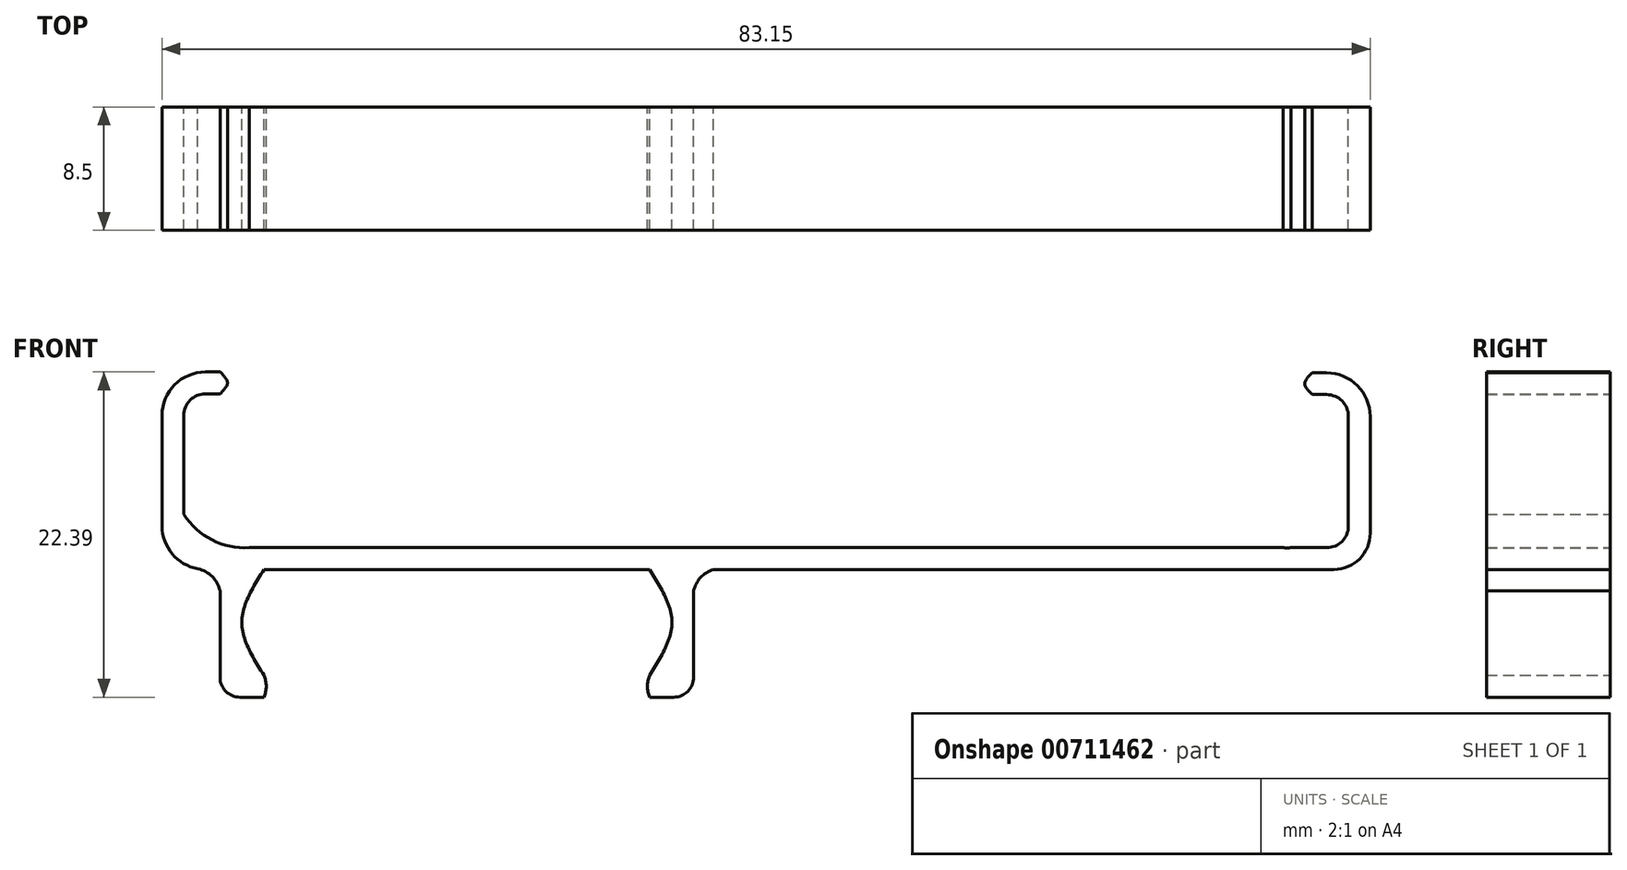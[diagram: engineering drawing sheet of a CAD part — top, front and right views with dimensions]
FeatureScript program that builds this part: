
annotation { "Feature Type Name" : "Feature", "Feature Type Description" : "" }
export const myFeature = defineFeature(function(context is Context, id is Id, definition is map)
    precondition{}
    {
        {
            var Q0;
            Q0=qCreatedBy(makeId("Front.planeOp"),FACE);
            var sketch = newSketch(context, id + "F0", { "sketchPlane" : qUnion([Q0])});
            skLineSegment(sketch, "E0", {"start": v(-20.82, 0) * mm, "end": v(56.33, 0) * mm});
            skPoint(sketch, "E1.visualSharp", {"position": v(-22.32, 10.6) * mm});
            skPoint(sketch, "E2.visualSharp", {"position": v(57.83, 10.54) * mm});
            skPoint(sketch, "E3.visualSharp", {"position": v(57.68, 0) * mm});
            skArc(sketch, "E3.filletArc", {"start": v(56.33, 0) * mm, "mid": v(57.39, 0.44) * mm, "end": v(57.83, 1.5) * mm});
            skPoint(sketch, "E4.visualSharp", {"position": v(-22.32, 0) * mm});
            skArc(sketch, "E4.filletArc", {"start": v(-22.32, 1.5) * mm, "mid": v(-21.88, 0.44) * mm, "end": v(-20.82, 0) * mm});
            skArc(sketch, "E5.0", {"start": v(-23.82, 1.5) * mm, "mid": v(-22.8, -0.76) * mm, "end": v(-20.42, -1.47) * mm});
            skLineSegment(sketch, "E6.0", {"start": v(-18.33, -1.5) * mm, "end": v(56.58, -1.5) * mm});
            skLineSegment(sketch, "E7", {"start": v(-22.32, 1.5) * mm, "end": v(-22.32, -1.1) * mm, "construction": true});
            skLineSegment(sketch, "E8", {"start": v(-19.83, -2.98) * mm, "end": v(-18.33, -2.98) * mm, "construction": true});
            skLineSegment(sketch, "E9", {"start": v(-18.33, -1.5) * mm, "end": v(-18.33, -8.79) * mm});
            skLineSegment(sketch, "E10", {"start": v(-18.33, -8.79) * mm, "end": v(-16.81, -8.79) * mm});
            skLineSegment(sketch, "E11", {"start": v(-20.42, -1.47) * mm, "end": v(-18.33, -1.5) * mm});
            skFitSpline(sketch, "E12", {"points": [v(-16.81, -8.79) * mm, v(-18.33, -5.14) * mm, v(-16.81, -1.5) * mm], "startDerivative": vector(-4.56, 7.29) * mm, "endDerivative": vector(4.56, 7.29) * mm});
            skLineSegment(sketch, "E13.0", {"start": v(-18.33, -10.29) * mm, "end": v(-16.81, -10.29) * mm});
            skLineSegment(sketch, "E14.0", {"start": v(-19.83, -1.5) * mm, "end": v(-19.83, -8.79) * mm});
            skLineSegment(sketch, "E15", {"start": v(-19.83, -8.79) * mm, "end": v(-19.83, -8.91) * mm});
            skLineSegment(sketch, "E16", {"start": v(-18.33, -10.29) * mm, "end": v(-18.46, -10.29) * mm});
            skArc(sketch, "E17", {"start": v(-19.83, -2.98) * mm, "mid": v(-20.4, -1.96) * mm, "end": v(-21.43, -1.44) * mm});
            skArc(sketch, "E18", {"start": v(-16.81, -10.29) * mm, "mid": v(-16.65, -9.54) * mm, "end": v(-16.81, -8.79) * mm});
            skPoint(sketch, "E19.visualSharp", {"position": v(-19.83, -10.29) * mm});
            skArc(sketch, "E19.filletArc", {"start": v(-19.83, -8.91) * mm, "mid": v(-19.43, -9.89) * mm, "end": v(-18.46, -10.29) * mm});
            skLineSegment(sketch, "E20", {"start": v(-18.33, -5.14) * mm, "end": v(-3.33, -5.14) * mm, "construction": true});
            skPoint(sketch, "E21.start.orphan", {"position": v(-3.33, -1.5) * mm});
            skLineSegment(sketch, "E22", {"start": v(-3.33, -1.5) * mm, "end": v(-3.33, -10.67) * mm, "construction": true});
            skLineSegment(sketch, "E23.MirrorCS", {"start": v(11.27, -10.29) * mm, "end": v(11.39, -10.29) * mm});
            skLineSegment(sketch, "E24.MirrorCS", {"start": v(12.77, -8.79) * mm, "end": v(12.77, -8.91) * mm});
            skLineSegment(sketch, "E25.MirrorCS", {"start": v(11.27, -8.79) * mm, "end": v(9.74, -8.79) * mm});
            skArc(sketch, "E26.MirrorCS", {"start": v(12.77, -8.91) * mm, "mid": v(12.36, -9.89) * mm, "end": v(11.39, -10.29) * mm});
            skLineSegment(sketch, "E27.MirrorCS", {"start": v(11.27, -10.29) * mm, "end": v(9.74, -10.29) * mm});
            skPoint(sketch, "E28.MirrorP", {"position": v(12.77, -10.29) * mm});
            skLineSegment(sketch, "E29.MirrorCS", {"start": v(11.67, -5.14) * mm, "end": v(-3.33, -5.14) * mm, "construction": true});
            skLineSegment(sketch, "E30.MirrorCS", {"start": v(12.77, -1.5) * mm, "end": v(12.77, -8.79) * mm});
            skFitSpline(sketch, "E31.MirrorCS", {"points": [v(9.74, -8.79) * mm, v(11.27, -5.14) * mm, v(9.74, -1.5) * mm], "startDerivative": vector(4.56, 7.29) * mm, "endDerivative": vector(-4.56, 7.29) * mm});
            skLineSegment(sketch, "E32.MirrorCS", {"start": v(11.27, -1.5) * mm, "end": v(11.27, -8.79) * mm});
            skArc(sketch, "E33.MirrorCS", {"start": v(9.74, -10.29) * mm, "mid": v(9.59, -9.54) * mm, "end": v(9.74, -8.79) * mm});
            skLineSegment(sketch, "E34.MirrorCS", {"start": v(12.77, -2.98) * mm, "end": v(11.27, -2.98) * mm, "construction": true});
            skArc(sketch, "E35.MirrorCS", {"start": v(12.77, -2.98) * mm, "mid": v(13.33, -1.96) * mm, "end": v(14.37, -1.44) * mm});
            skLineSegment(sketch, "E36", {"start": v(59.33, 1.4) * mm, "end": v(59.33, 1) * mm});
            skLineSegment(sketch, "E37", {"start": v(56.83, -1.5) * mm, "end": v(56.58, -1.5) * mm});
            skPoint(sketch, "E38.visualSharp", {"position": v(59.33, -1.5) * mm});
            skArc(sketch, "E38.filletArc", {"start": v(56.83, -1.5) * mm, "mid": v(58.6, -0.77) * mm, "end": v(59.33, 1) * mm});
            skLineSegment(sketch, "E39", {"start": v(-20.82, 10.6) * mm, "end": v(-19.82, 10.6) * mm});
            skLineSegment(sketch, "E40", {"start": v(-19.82, 10.6) * mm, "end": v(-19.82, 12.1) * mm, "construction": true});
            skFitSpline(sketch, "E41", {"points": [v(-19.82, 12.1) * mm, v(-19.32, 11.35) * mm, v(-19.82, 10.6) * mm], "startDerivative": vector(1.5, -1.5) * mm, "endDerivative": vector(-1.5, -1.5) * mm});
            skLineSegment(sketch, "E42", {"start": v(-22.32, 1.5) * mm, "end": v(-22.32, 9.1) * mm});
            skLineSegment(sketch, "E43", {"start": v(-19.82, 12.1) * mm, "end": v(-20.82, 12.1) * mm});
            skLineSegment(sketch, "E44", {"start": v(-23.82, 9.1) * mm, "end": v(-23.82, 1.5) * mm});
            skArc(sketch, "E45.filletArc", {"start": v(-20.82, 10.6) * mm, "mid": v(-21.88, 10.16) * mm, "end": v(-22.32, 9.1) * mm});
            skPoint(sketch, "E46.visualSharp", {"position": v(-23.82, 12.1) * mm});
            skArc(sketch, "E46.filletArc", {"start": v(-20.82, 12.1) * mm, "mid": v(-22.94, 11.22) * mm, "end": v(-23.82, 9.1) * mm});
            skLineSegment(sketch, "E47", {"start": v(57.83, 1.5) * mm, "end": v(57.83, 9.04) * mm});
            skLineSegment(sketch, "E48.trimOffspring", {"start": v(55.33, 10.54) * mm, "end": v(56.33, 10.54) * mm});
            skLineSegment(sketch, "E49", {"start": v(55.33, 12.04) * mm, "end": v(55.33, 10.54) * mm});
            skLineSegment(sketch, "E50", {"start": v(59.33, 1.4) * mm, "end": v(59.33, 9.04) * mm});
            skLineSegment(sketch, "E51", {"start": v(55.33, 12.04) * mm, "end": v(56.33, 12.04) * mm});
            skArc(sketch, "E52.filletArc", {"start": v(57.83, 9.04) * mm, "mid": v(57.39, 10.1) * mm, "end": v(56.33, 10.54) * mm});
            skPoint(sketch, "E53.visualSharp", {"position": v(59.33, 12.04) * mm});
            skArc(sketch, "E53.filletArc", {"start": v(59.33, 9.04) * mm, "mid": v(58.45, 11.16) * mm, "end": v(56.33, 12.04) * mm});
            skLineSegment(sketch, "E54", {"start": v(-19.32, 11.35) * mm, "end": v(-19.82, 11.35) * mm, "construction": true});
            skPoint(sketch, "E55.start.orphan", {"position": v(55.33, 11.3) * mm});
            skLineSegment(sketch, "E56", {"start": v(55.33, 11.3) * mm, "end": v(54.83, 11.3) * mm, "construction": true});
            skFitSpline(sketch, "E57", {"points": [v(55.33, 12.04) * mm, v(54.83, 11.3) * mm, v(55.33, 10.54) * mm], "startDerivative": vector(-1.5, -1.5) * mm, "endDerivative": vector(1.5, -1.5) * mm});
            skLineSegment(sketch, "E58", {"start": v(-22.32, 5.3) * mm, "end": v(57.83, 5.3) * mm, "construction": true});
            skPoint(sketch, "E59.end.orphan", {"position": v(-19.82, 6.72) * mm});
            skLineSegment(sketch, "E60", {"start": v(-19.82, 10.6) * mm, "end": v(-19.82, 0) * mm, "construction": true});
            skLineSegment(sketch, "E61", {"start": v(55.33, 10.54) * mm, "end": v(55.33, 0) * mm, "construction": true});
            skLineSegment(sketch, "E62", {"start": v(-20.82, 2.3) * mm, "end": v(-22.32, 2.3) * mm, "construction": true});
            skLineSegment(sketch, "E63", {"start": v(-22.32, 2.3) * mm, "end": v(-17.82, 2.3) * mm, "construction": true});
            skArc(sketch, "E64", {"start": v(-22.32, 2.3) * mm, "mid": v(-20.39, 0.54) * mm, "end": v(-17.82, 0) * mm});
            skLineSegment(sketch, "E65", {"start": v(57.83, 2.3) * mm, "end": v(53.33, 2.3) * mm, "construction": true});
            skArc(sketch, "E66", {"start": v(53.33, 0) * mm, "mid": v(55.9, 0.54) * mm, "end": v(57.83, 2.3) * mm});
            skSolve(sketch);
        }
        {
            var Q0;
            Q0=makeQuery(id+"F0.imprint","IMPRINT",FACE,{"disambiguationData":[TD([[makeQuery(id+"F0.imprint","IMPRINT",EDGE,{"derivedFrom":sQuery(id+"F0.wireOp",EDGE,"E23.MirrorCS")}),1.0]])]});
            var Q1;
            {var subQ9=sQuery(id+"F0.wireOp",EDGE,"E10");Q1=makeQuery(id+"F0.imprint","IMPRINT",FACE,{"disambiguationData":[TD([[makeQuery(id+"F0.imprint","IMPRINT",EDGE,{"derivedFrom":subQ9}),-1.0]])]});}
            var Q2;
            {var subQ0=sQuery(id+"F0.wireOp",EDGE,"E30.MirrorCS");var subQ1=sQuery(id+"F0.wireOp",EDGE,"E6.0");var subQ2=makeQuery(id+"F0.imprint","INTERSECT",VERTEX,{"derivedFrom":[subQ1,subQ0]});Q2=makeQuery(id+"F0.imprint","IMPRINT",FACE,{"disambiguationData":[TD([[makeQuery(id+"F0.imprint","IMPRINT",EDGE,{"disambiguationData":[TD([[subQ2,-1.0]])],"derivedFrom":subQ1}),-1.0]])]});}
            var Q3;
            {var subQ0=sQuery(id+"F0.wireOp",EDGE,"E10");Q3=makeQuery(id+"F0.imprint","IMPRINT",FACE,{"disambiguationData":[TD([[makeQuery(id+"F0.imprint","IMPRINT",EDGE,{"derivedFrom":subQ0}),1.0]])]});}
            var Q4;
            {var subQ0=sQuery(id+"F0.wireOp",EDGE,"E31.MirrorCS");var subQ1=sQuery(id+"F0.wireOp",EDGE,"E6.0");var subQ2=makeQuery(id+"F0.imprint","INTERSECT",VERTEX,{"derivedFrom":[subQ1,subQ0]});Q4=makeQuery(id+"F0.imprint","IMPRINT",FACE,{"disambiguationData":[TD([[makeQuery(id+"F0.imprint","IMPRINT",EDGE,{"disambiguationData":[TD([[subQ2,-1.0]])],"derivedFrom":subQ1}),-1.0]])]});}
            var Q5;
            {var subQ0=sQuery(id+"F0.wireOp",EDGE,"E17");var subQ1=sQuery(id+"F0.wireOp",EDGE,"E5.0");var subQ2=makeQuery(id+"F0.imprint","INTERSECT",VERTEX,{"disambiguationData":[OD(0.0)],"derivedFrom":[subQ1,subQ0]});Q5=makeQuery(id+"F0.imprint","IMPRINT",FACE,{"disambiguationData":[TD([[makeQuery(id+"F0.imprint","IMPRINT",EDGE,{"disambiguationData":[TD([[subQ2,-1.0]])],"derivedFrom":subQ1}),1.0]])]});}
            var Q6;
            Q6=makeQuery(id+"F0.imprint","IMPRINT",FACE,{"disambiguationData":[TD([[makeQuery(id+"F0.imprint","IMPRINT",EDGE,{"derivedFrom":sQuery(id+"F0.wireOp",EDGE,"E49")}),-1.0]])]});
            var Q7;
            {var subQ1=sQuery(id+"F0.wireOp",EDGE,"E6.0");var subQ3=sQuery(id+"F0.wireOp",EDGE,"E12");var subQ4=makeQuery(id+"F0.imprint","INTERSECT",VERTEX,{"derivedFrom":[subQ1,subQ3]});Q7=makeQuery(id+"F0.imprint","IMPRINT",FACE,{"disambiguationData":[TD([[makeQuery(id+"F0.imprint","IMPRINT",EDGE,{"disambiguationData":[TD([[subQ4,1.0]])],"derivedFrom":subQ3}),1.0]])]});}
            var Q8;
            {var subQ0=sQuery(id+"F0.wireOp",EDGE,"E25.MirrorCS");Q8=makeQuery(id+"F0.imprint","IMPRINT",FACE,{"disambiguationData":[TD([[makeQuery(id+"F0.imprint","IMPRINT",EDGE,{"derivedFrom":subQ0}),-1.0]])]});}
            var Q9;
            {var subQ7=sQuery(id+"F0.wireOp",EDGE,"E3.filletArc");Q9=makeQuery(id+"F0.imprint","IMPRINT",FACE,{"disambiguationData":[TD([[makeQuery(id+"F0.imprint","IMPRINT",EDGE,{"derivedFrom":subQ7}),-1.0]])]});}
            var Q10;
            {var subQ0=sQuery(id+"F0.wireOp",EDGE,"E3.filletArc");Q10=makeQuery(id+"F0.imprint","IMPRINT",FACE,{"disambiguationData":[TD([[makeQuery(id+"F0.imprint","IMPRINT",EDGE,{"derivedFrom":subQ0}),1.0]])]});}
            var Q11;
            {var subQ0=sQuery(id+"F0.wireOp",EDGE,"E4.filletArc");Q11=makeQuery(id+"F0.imprint","IMPRINT",FACE,{"disambiguationData":[TD([[makeQuery(id+"F0.imprint","IMPRINT",EDGE,{"derivedFrom":subQ0}),1.0]])]});}
            extrude(context, id + "F1", {"entities" : qUnion([Q0, Q1, Q2, Q3, Q4, Q5, Q6, Q7, Q8, Q9, Q10, Q11]), "endBound" : BoundingType.SYMMETRIC, "depth" : 8.5 * mm, "offsetDistance" : 25 * mm});
        }
    });
